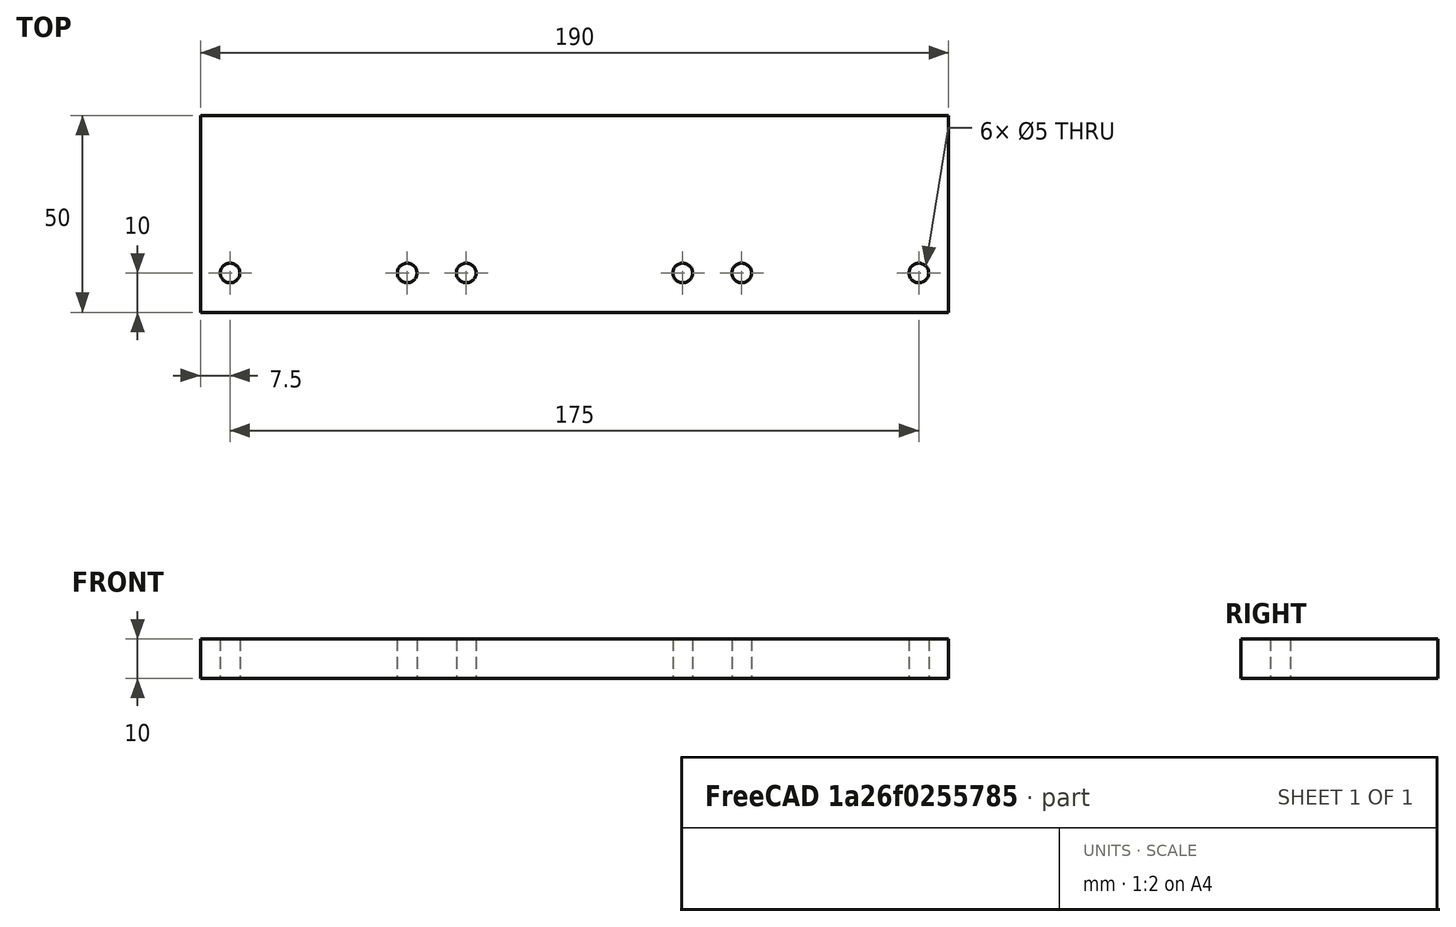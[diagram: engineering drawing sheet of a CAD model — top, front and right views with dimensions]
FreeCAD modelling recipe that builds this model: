
FCSTD DOCUMENT  (FreeCAD 0.17R13528 (Git))
Label: plate8
License: All rights reserved
LicenseURL: http://en.wikipedia.org/wiki/All_rights_reserved
objects: TechDraw::DrawViewDimension×16, PartDesign::LinearPattern×5, TechDraw::DrawProjGroupItem×3, Sketcher::SketchObject×2, PartDesign::Pad×1, PartDesign::Hole×1, PartDesign::Body×1, TechDraw::DrawSVGTemplate×1, TechDraw::DrawProjGroup×1, TechDraw::DrawViewAnnotation×1, TechDraw::DrawPage×1
note: 12 computed .brp shape members not serialized (recipe doc carries the construction recipe); baked Part::Feature solids carry a one-line shape summary decoded from their .brp

FEATURE [Sketcher::SketchObject] Sketch
  MapMode = 5
  Support = -> [XY_Plane]
  sketch-geometry (4):
    g0: LineSegment StartX=0 StartY=0 StartZ=0 EndX=190 EndY=0 EndZ=0
    g1: LineSegment StartX=190 StartY=0 StartZ=0 EndX=190 EndY=50 EndZ=0
    g2: LineSegment StartX=190 StartY=50 StartZ=0 EndX=0 EndY=50 EndZ=0
    g3: LineSegment StartX=0 StartY=50 StartZ=0 EndX=0 EndY=0 EndZ=0
  constraints (11):
    c: Coincident(g0,g1)
    c: Coincident(g1,g2)
    c: Coincident(g2,g3)
    c: Coincident(g3,g0)
    c: Horizontal(g0)
    c: Horizontal(g2)
    c: Vertical(g1)
    c: Vertical(g3)
    c: Coincident(g0,g-1)
    c: DistanceX(g0,g0) = 190
    c: DistanceY(g3,g3) = 50
FEATURE [PartDesign::Pad] Pad
  Length = 10
  Length2 = 100
  Profile = -> Sketch
  Type = 0
FEATURE [Sketcher::SketchObject] Sketch001
  MapMode = 5
  Placement = pos=(0,0,10) rot=(0,0,1;0rad)
  Support = -> [Pad]
  sketch-geometry (1):
    g0: Circle CenterX=7.5 CenterY=10 CenterZ=0 NormalX=0 NormalY=0 NormalZ=1 AngleXU=0 Radius=3
  constraints (2):
    c: Distance(g0,g-1) = 10
    c: Distance(g0,g-2) = 7.5
FEATURE [PartDesign::Hole] Hole
  BaseFeature = -> Pad
  Depth = 25
  DepthType = 1
  Diameter = 5
  DrillPoint = 0
  DrillPointAngle = 118
  HoleCutCountersinkAngle = 90
  HoleCutDepth = 0
  HoleCutDiameter = 6
  HoleCutType = 0
  ModelActualThread = false
  Profile = -> Sketch001
  Tapered = false
  TaperedAngle = 90
  ThreadAngle = 60
  ThreadClass = 0
  ThreadCutOffInner = 0.108253
  ThreadCutOffOuter = 0.216506
  ThreadDirection = 1
  ThreadFit = 0
  ThreadPitch = 1
  ThreadSize = 7
  ThreadType = 1
  Threaded = true
FEATURE [PartDesign::LinearPattern] LinearPattern
  BaseFeature = -> Hole
  Direction = -> Sketch001 [H_Axis]
  Length = 45
  Occurrences = 2
  Originals = -> [Hole]
FEATURE [PartDesign::LinearPattern] LinearPattern001
  BaseFeature = -> LinearPattern
  Direction = -> Sketch001 [H_Axis]
  Length = 60
  Occurrences = 2
  Originals = -> [Hole]
FEATURE [PartDesign::LinearPattern] LinearPattern002
  BaseFeature = -> LinearPattern001
  Direction = -> Sketch001 [H_Axis]
  Length = 115
  Occurrences = 2
  Originals = -> [Hole]
FEATURE [PartDesign::LinearPattern] LinearPattern003
  BaseFeature = -> LinearPattern002
  Direction = -> Sketch001 [H_Axis]
  Length = 130
  Occurrences = 2
  Originals = -> [Hole]
FEATURE [PartDesign::LinearPattern] LinearPattern004
  BaseFeature = -> LinearPattern003
  Direction = -> Sketch001 [H_Axis]
  Length = 175
  Occurrences = 2
  Originals = -> [Hole]
FEATURE [PartDesign::Body] Body
  Group = -> [Sketch,Pad,Sketch001,Hole,LinearPattern,LinearPattern001,LinearPattern002,LinearPattern003,LinearPattern004]
  Origin = -> Origin
  Tip = -> LinearPattern004
FEATURE [TechDraw::DrawSVGTemplate] Template
  EditableTexts = Designed_by_Name=Lukas Winter; FC-Date=27.08.2018; FC-SC=1:2; FC-SH=1/1; FC-Title=COSI Measure v1.0; Subtitle=Mechanical Assembly - plate 8
  Height = 210
  Orientation = 1
  Width = 297
FEATURE [TechDraw::DrawProjGroupItem] ProjItem  label="Front"
  CoarseView = false
  Direction = (0,-1,0)
  Focus = 100
  HardHidden = false
  IsoCount = 0
  IsoHidden = false
  IsoVisible = false
  LockPosition = false
  Perspective = false
  Rotation = 0
  RotationVector = (1,0,0)
  ScaleType = 0
  SeamHidden = false
  SeamVisible = false
  SmoothHidden = false
  SmoothVisible = false
  Source = -> [Body]
  Type = 0
  X = 0
  Y = -42.5
FEATURE [TechDraw::DrawProjGroupItem] ProjItem001  label="Bottom"
  CoarseView = false
  Direction = (0,0,-1)
  Focus = 100
  HardHidden = false
  IsoCount = 0
  IsoHidden = false
  IsoVisible = false
  LockPosition = false
  Perspective = false
  Rotation = 0
  RotationVector = (1,0,0)
  ScaleType = 0
  SeamHidden = false
  SeamVisible = false
  SmoothHidden = false
  SmoothVisible = false
  Source = -> [Body]
  Type = 5
  X = 0
  Y = -40
FEATURE [TechDraw::DrawProjGroupItem] ProjItem002  label="Right"
  CoarseView = false
  Direction = (1,0,0)
  Focus = 100
  HardHidden = false
  IsoCount = 0
  IsoHidden = false
  IsoVisible = false
  LockPosition = false
  Perspective = false
  Rotation = 0
  RotationVector = (0,-1,0)
  ScaleType = 0
  SeamHidden = false
  SeamVisible = false
  SmoothHidden = false
  SmoothVisible = false
  Source = -> [Body]
  Type = 2
  X = 110
  Y = 0
FEATURE [TechDraw::DrawProjGroup] ProjGroup
  Anchor = -> ProjItem
  AutoDistribute = true
  CubeDirs = (1) [(0,0,0)]
  CubeRotations = (1) [(0,0,0)]
  LockPosition = false
  ProjectionType = 2
  Rotation = 0
  Scale = 0.5
  ScaleType = 1
  Source = -> [Body]
  Views = -> [ProjItem001,ProjItem,ProjItem002]
  X = 94.2716
  Y = 147.13
  spacingX = 15
  spacingY = 15
FEATURE [TechDraw::DrawViewDimension] Dimension
  FormatSpec = %.2f
  LockPosition = false
  MeasureType = 1
  References2D = -> [ProjItem]
  Rotation = 0
  ScaleType = 0
  Type = 1
  X = 0
  Y = 16.2037
FEATURE [TechDraw::DrawViewDimension] Dimension001
  FormatSpec = %.2f
  LockPosition = false
  MeasureType = 1
  References2D = -> [ProjItem002]
  Rotation = 0
  ScaleType = 0
  Type = 2
  X = 36.7284
  Y = -14.0432
FEATURE [TechDraw::DrawViewDimension] Dimension002
  FormatSpec = %.2f
  LockPosition = false
  MeasureType = 1
  References2D = -> [ProjItem002]
  Rotation = 0
  ScaleType = 0
  Type = 1
  X = 0
  Y = 15.9877
FEATURE [TechDraw::DrawViewDimension] Dimension003
  FormatSpec = %.2f
  LockPosition = false
  MeasureType = 1
  References2D = -> [ProjItem001]
  Rotation = 0
  ScaleType = 0
  Type = 1
  X = 60.299
  Y = -3.99703
FEATURE [TechDraw::DrawViewDimension] Dimension004
  FormatSpec = %.2f
  LockPosition = false
  MeasureType = 1
  References2D = -> [ProjItem001]
  Rotation = 0
  ScaleType = 0
  Type = 1
  X = 32.5969
  Y = 19.1747
FEATURE [TechDraw::DrawViewDimension] Dimension005
  FormatSpec = %.2f
  LockPosition = false
  MeasureType = 1
  References2D = -> [ProjItem001]
  Rotation = 0
  ScaleType = 0
  Type = 1
  X = 2.32835
  Y = 25.4749
FEATURE [TechDraw::DrawViewDimension] Dimension006
  FormatSpec = %.2f
  LockPosition = false
  MeasureType = 1
  References2D = -> [ProjItem001]
  Rotation = 0
  ScaleType = 0
  Type = 1
  X = -61.222
  Y = -3.42405
FEATURE [TechDraw::DrawViewDimension] Dimension007
  FormatSpec = %.2f
  LockPosition = false
  MeasureType = 1
  References2D = -> [ProjItem001]
  Rotation = 0
  ScaleType = 0
  Type = 1
  X = -30.9534
  Y = 23.4205
FEATURE [TechDraw::DrawViewDimension] Dimension008
  FormatSpec = %.2f
  LockPosition = false
  MeasureType = 1
  References2D = -> [ProjItem001]
  Rotation = 0
  ScaleType = 0
  Type = 1
  X = -1.91747
  Y = 19.0377
FEATURE [TechDraw::DrawViewDimension] Dimension009 .. Dimension012  x4 (patterned run collapsed; names and placements below)
  FormatSpec = %.2f
  LockPosition = false
  MeasureType = 1
  References2D = -> [ProjItem001]
  Rotation = 0
  ScaleType = 0
  Type = 5
  X = 0
  Y = 0
FEATURE [TechDraw::DrawViewDimension] Dimension013
  FormatSpec = %.2f
  LockPosition = false
  MeasureType = 1
  References2D = -> [ProjItem001]
  Rotation = 0
  ScaleType = 0
  Type = 5
  X = -16.1615
  Y = -4.38278
FEATURE [TechDraw::DrawViewDimension] Dimension014
  FormatSpec = %.2f
  LockPosition = false
  MeasureType = 1
  References2D = -> [ProjItem001]
  Rotation = 0
  ScaleType = 0
  Type = 5
  X = 10.957
  Y = -5.7524
FEATURE [TechDraw::DrawViewDimension] Dimension015
  FormatSpec = %.2f
  LockPosition = false
  MeasureType = 1
  References2D = -> [ProjItem001]
  Rotation = 0
  ScaleType = 0
  Type = 2
  X = -77.9841
  Y = 3.06366
FEATURE [TechDraw::DrawViewAnnotation] Annotation
  Font = osifont
  LineSpace = 80
  LockPosition = false
  MaxWidth = -1
  Rotation = 0
  ScaleType = 0
  Text = Note: For the holes (d=5mm) make a thread M6. | Alternatively you can also make a through hole | (d=6.6mm) and use a longer M6 screw together  | with a screw nut on the other end.
  TextSize = 4
  TextStyle = 0
  X = 66.8333
  Y = 33.2716
FEATURE [TechDraw::DrawPage] Page
  KeepUpdated = true
  ProjectionType = 0
  Template = -> Template
  Views = -> [ProjGroup,Dimension,Dimension001,Dimension002,Dimension003,Dimension004,Dimension005,Dimension006,Dimension007,Dimension008,Dimension009,Dimension010,Dimension011,Dimension012,Dimension013,Dimension014,Dimension015,Annotation]
